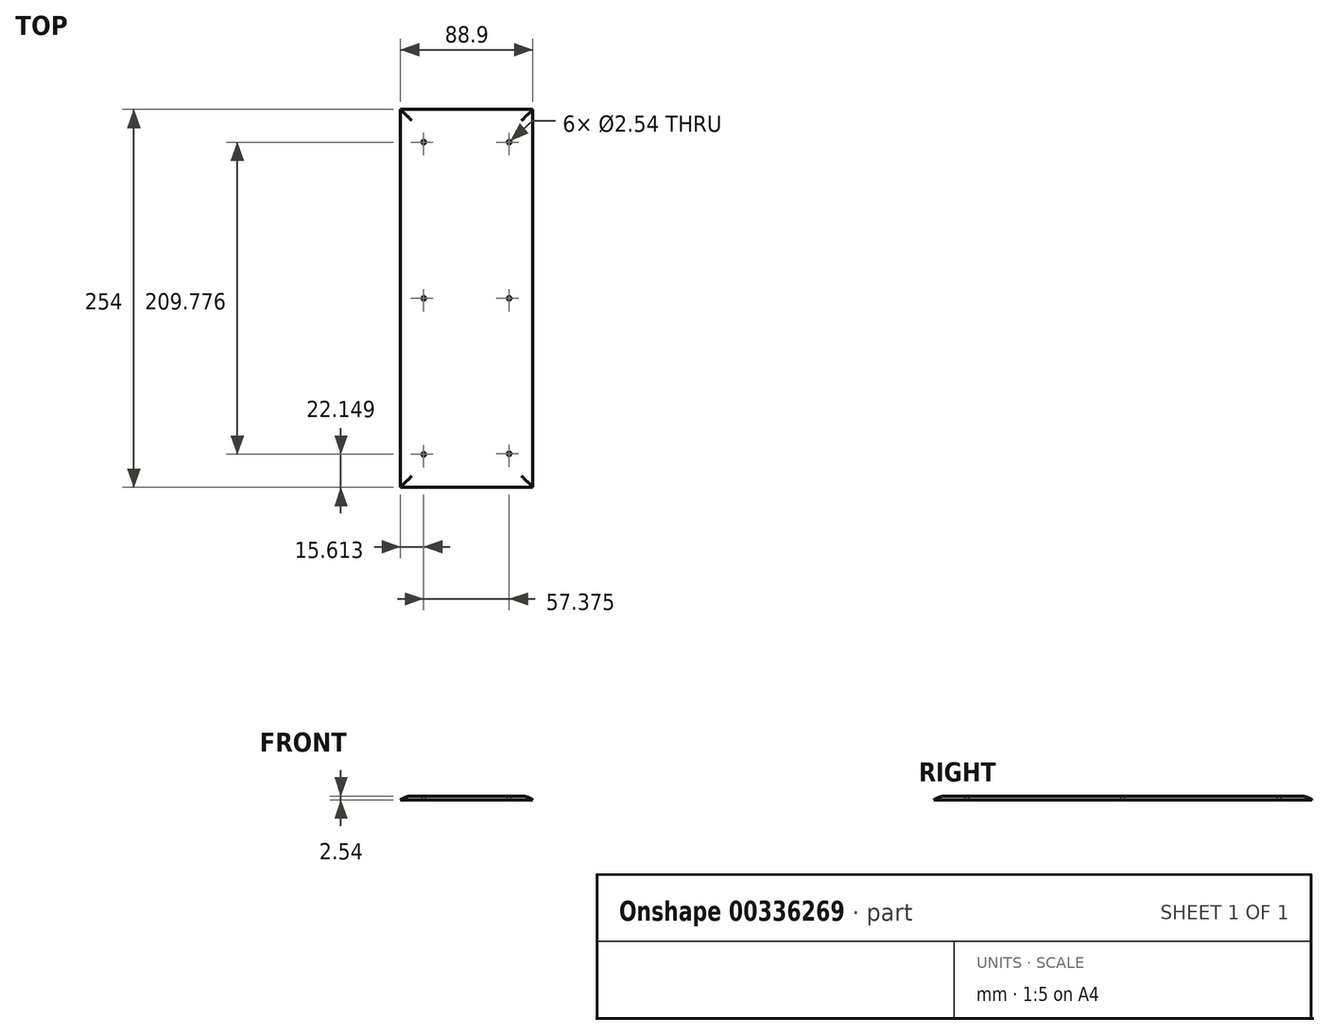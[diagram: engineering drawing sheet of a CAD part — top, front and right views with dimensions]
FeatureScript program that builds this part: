
annotation { "Feature Type Name" : "Feature", "Feature Type Description" : "" }
export const myFeature = defineFeature(function(context is Context, id is Id, definition is map)
    precondition{}
    {
        {
            var Q0;
            Q0=qCreatedBy(makeId("Top.planeOp"),FACE);
            var sketch = newSketch(context, id + "F0", { "sketchPlane" : qUnion([Q0])});
            skLineSegment(sketch, "E0.bottom", {"start": v(-44.45, 127) * mm, "end": v(44.45, 127) * mm});
            skLineSegment(sketch, "E0.top", {"start": v(-44.45, -127) * mm, "end": v(44.45, -127) * mm});
            skLineSegment(sketch, "E0.left", {"start": v(-44.45, 127) * mm, "end": v(-44.45, -127) * mm});
            skLineSegment(sketch, "E0.right", {"start": v(44.45, 127) * mm, "end": v(44.45, -127) * mm});
            skPoint(sketch, "E0.middle", {"position": v(0, 0) * mm});
            skSolve(sketch);
        }
        {
            var Q0;
            Q0=makeQuery(id+"F0.imprint","IMPRINT",FACE,{"disambiguationData":[TD([[makeQuery(id+"F0.imprint","IMPRINT",EDGE,{"derivedFrom":sQuery(id+"F0.wireOp",EDGE,"E0.bottom")}),-1.0]])]});
            extrude(context, id + "F1", {"entities" : qUnion([Q0]), "depth" : 2.54 * mm});
        }
        {
            var Q0;
            Q0=makeQuery(id+"F1.opExtrude","CAP_FACE",FACE,{"disambiguationData":[OSD([sQuery(id+"F0.wireOp",EDGE,"E0.bottom"),sQuery(id+"F0.wireOp",EDGE,"E0.top"),sQuery(id+"F0.wireOp",EDGE,"E0.left"),sQuery(id+"F0.wireOp",EDGE,"E0.right")])],"isStart":false});
            fillet(context, id + "F2", {"entities" : qUnion([Q0]), "radius" : 12.7 * mm, "tangentPropagation" : true, "allowEdgeOverflow" : false});
        }
        {
            var Q0;
            Q0=makeQuery(id+"F1.opExtrude","CAP_FACE",FACE,{"disambiguationData":[OSD([sQuery(id+"F0.wireOp",EDGE,"E0.bottom"),sQuery(id+"F0.wireOp",EDGE,"E0.top"),sQuery(id+"F0.wireOp",EDGE,"E0.left"),sQuery(id+"F0.wireOp",EDGE,"E0.right")])],"isStart":false});
            var sketch = newSketch(context, id + "F3", { "sketchPlane" : qUnion([Q0])});
            skLineSegment(sketch, "E1.bottom", {"start": v(-28.57, 104.78) * mm, "end": v(28.58, 104.78) * mm});
            skLineSegment(sketch, "E1.top", {"start": v(-28.58, -104.78) * mm, "end": v(28.57, -104.78) * mm});
            skLineSegment(sketch, "E1.left", {"start": v(-28.57, 104.78) * mm, "end": v(-28.58, -104.78) * mm});
            skLineSegment(sketch, "E1.right", {"start": v(28.58, 104.78) * mm, "end": v(28.57, -104.78) * mm});
            skPoint(sketch, "E1.middle", {"position": v(0, 0) * mm});
            skSolve(sketch);
        }
        {
            var Q0;
            Q0=makeQuery(id+"F3.imprint","IMPRINT",FACE,{"disambiguationData":[TD([[makeQuery(id+"F3.imprint","IMPRINT",EDGE,{"derivedFrom":sQuery(id+"F3.wireOp",EDGE,"E1.bottom")}),-1.0]])]});
            var sketch = newSketch(context, id + "F4", { "sketchPlane" : qUnion([Q0])});
            skPoint(sketch, "E2", {"position": v(-28.84, 104.93) * mm});
            skPoint(sketch, "E3", {"position": v(28.54, 104.93) * mm});
            skPoint(sketch, "E4", {"position": v(28.54, 0) * mm});
            skPoint(sketch, "E5", {"position": v(-28.84, 0) * mm});
            skPoint(sketch, "E6", {"position": v(-28.84, -93.38) * mm});
            skPoint(sketch, "E7", {"position": v(28.54, -104.5) * mm});
            skPoint(sketch, "E8", {"position": v(-28.84, -104.85) * mm});
            skSolve(sketch);
        }
        {
            var Q0;
            Q0=sQuery(id+"F4.wireOp",VERTEX,"E2");
            var Q1;
            Q1=sQuery(id+"F4.wireOp",VERTEX,"E3");
            var Q2;
            Q2=sQuery(id+"F4.wireOp",VERTEX,"E4");
            var Q3;
            Q3=sQuery(id+"F4.wireOp",VERTEX,"E5");
            var Q4;
            Q4=sQuery(id+"F4.wireOp",VERTEX,"E8");
            var Q5;
            Q5=sQuery(id+"F4.wireOp",VERTEX,"E7");
            var Q6;
            Q6=makeQuery(id+"F1.opExtrude","SWEPT_BODY",BODY,{"disambiguationData":[OSD([sQuery(id+"F0.wireOp",EDGE,"E0.bottom"),sQuery(id+"F0.wireOp",EDGE,"E0.top"),sQuery(id+"F0.wireOp",EDGE,"E0.left"),sQuery(id+"F0.wireOp",EDGE,"E0.right")])]});
            hole(context, id + "F5", {"style" : HoleStyle.SIMPLE, "endStyle" : HoleEndStyle.BLIND, "holeDiameter" : 2.54 * mm, "holeDepth" : 5.08 * mm, "tappedDepth" : 101.6 * mm, "tapClearance" : 3, "locations" : qUnion([Q0, Q1, Q2, Q3, Q4, Q5]), "scope" : qUnion([Q6])});
        }
    });
